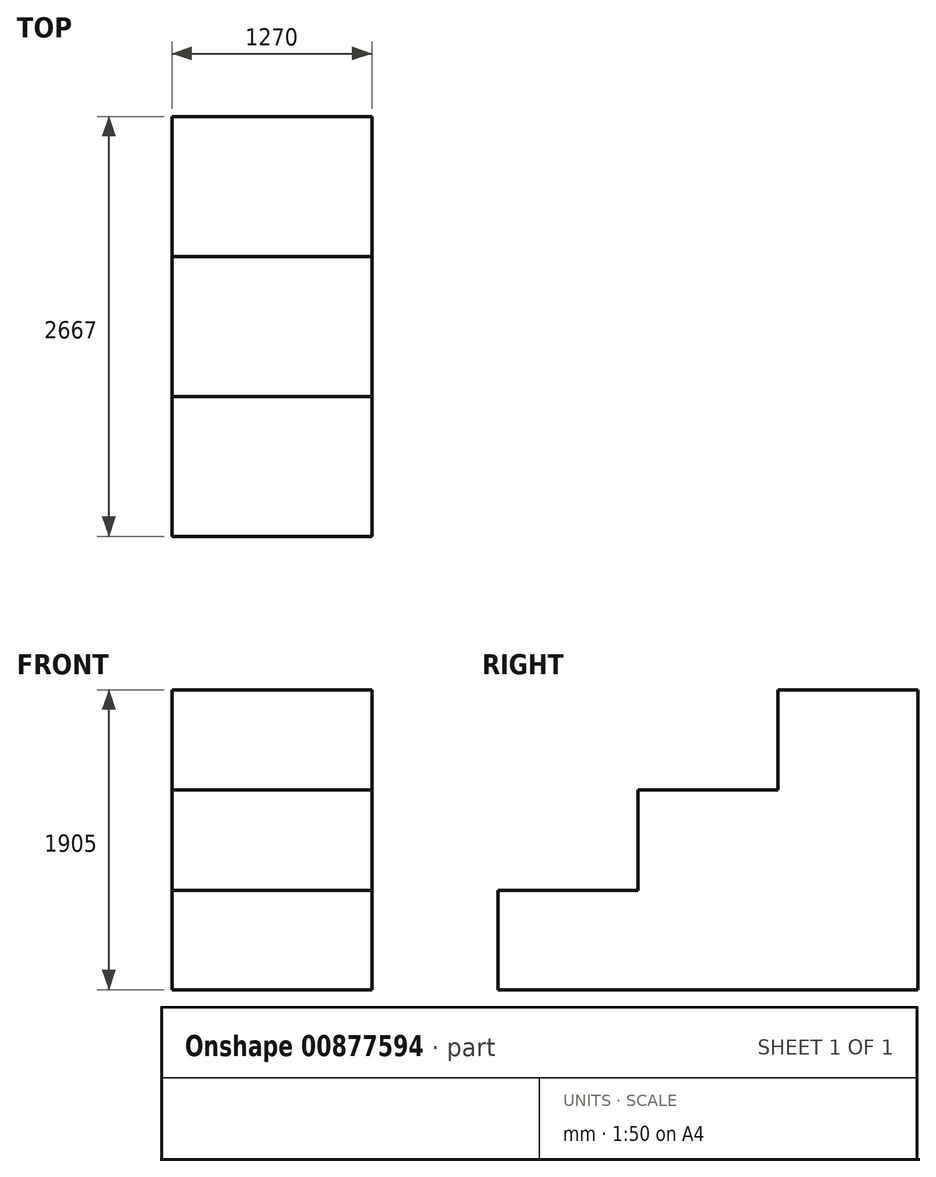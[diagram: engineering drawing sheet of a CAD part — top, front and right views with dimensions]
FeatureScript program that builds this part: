
annotation { "Feature Type Name" : "Feature", "Feature Type Description" : "" }
export const myFeature = defineFeature(function(context is Context, id is Id, definition is map)
    precondition{}
    {
        {
            var Q0;
            Q0=qCreatedBy(makeId("Front.planeOp"),FACE);
            var sketch = newSketch(context, id + "F0", { "sketchPlane" : qUnion([Q0])});
            skLineSegment(sketch, "E0.bottom", {"start": v(0, 0) * mm, "end": v(-1270, 0) * mm});
            skLineSegment(sketch, "E0.top", {"start": v(0, 1905) * mm, "end": v(-1270, 1905) * mm});
            skLineSegment(sketch, "E0.left", {"start": v(0, 0) * mm, "end": v(0, 1905) * mm});
            skLineSegment(sketch, "E0.right", {"start": v(-1270, 0) * mm, "end": v(-1270, 1905) * mm});
            skSolve(sketch);
        }
        {
            var Q0;
            Q0=makeQuery(id+"F0.imprint","IMPRINT",FACE,{"disambiguationData":[TD([[makeQuery(id+"F0.imprint","IMPRINT",EDGE,{"derivedFrom":sQuery(id+"F0.wireOp",EDGE,"E0.bottom")}),-1.0]])]});
            extrude(context, id + "F1", {"entities" : qUnion([Q0]), "depth" : 2667 * mm, "offsetDistance" : 25.4 * mm});
        }
        {
            var Q0;
            Q0=makeQuery(id+"F1.opExtrude","SWEPT_FACE",FACE,{"disambiguationData":[OSD([sQuery(id+"F0.wireOp",EDGE,"E0.left")])]});
            var sketch = newSketch(context, id + "F2", { "sketchPlane" : qUnion([Q0])});
            skLineSegment(sketch, "E1.bottom", {"start": v(-2667, 1264.99) * mm, "end": v(-1778, 1264.99) * mm});
            skLineSegment(sketch, "E1.top", {"start": v(-2667, 629.99) * mm, "end": v(-1778, 629.99) * mm});
            skLineSegment(sketch, "E1.left", {"start": v(-2667, 1264.99) * mm, "end": v(-2667, 629.99) * mm});
            skLineSegment(sketch, "E1.right", {"start": v(-1778, 1264.99) * mm, "end": v(-1778, 629.99) * mm});
            skSolve(sketch);
        }
        {
            var Q0;
            Q0=makeQuery(id+"F2.imprint","IMPRINT",FACE,{"disambiguationData":[TD([[makeQuery(id+"F2.imprint","IMPRINT",EDGE,{"derivedFrom":sQuery(id+"F2.wireOp",EDGE,"E1.bottom")}),-1.0]])]});
            extrude(context, id + "F3", {"entities" : qUnion([Q0]), "operationType" : NewBodyOperationType.REMOVE, "oppositeDirection" : true, "depth" : 1882.14 * mm, "offsetDistance" : 25.4 * mm});
        }
        {
            var Q0;
            Q0=makeQuery(id+"F1.opExtrude","SWEPT_FACE",FACE,{"disambiguationData":[OSD([sQuery(id+"F0.wireOp",EDGE,"E0.left")])]});
            var sketch = newSketch(context, id + "F4", { "sketchPlane" : qUnion([Q0])});
            skLineSegment(sketch, "E2", {"start": v(-1778, 1264.99) * mm, "end": v(-1778, 1905) * mm});
            skSolve(sketch);
        }
        {
            var Q0;
            {var subQ0=sQuery(id+"F4.wireOp",EDGE,"E2");Q0=makeQuery(id+"F4.imprint","IMPRINT",FACE,{"disambiguationData":[TD([[makeQuery(id+"F4.imprint","IMPRINT",EDGE,{"derivedFrom":subQ0}),1.0]])]});}
            extrude(context, id + "F5", {"entities" : qUnion([Q0]), "operationType" : NewBodyOperationType.REMOVE, "oppositeDirection" : true, "depth" : 2161.54 * mm, "offsetDistance" : 25.4 * mm});
        }
        {
            var Q0;
            Q0=makeQuery(id+"F1.opExtrude","SWEPT_FACE",FACE,{"disambiguationData":[OSD([sQuery(id+"F0.wireOp",EDGE,"E0.left")])]});
            var sketch = newSketch(context, id + "F6", { "sketchPlane" : qUnion([Q0])});
            skLineSegment(sketch, "E3.bottom", {"start": v(-1778, 1267.5) * mm, "end": v(-889, 1267.5) * mm});
            skLineSegment(sketch, "E3.top", {"start": v(-1778, 1905) * mm, "end": v(-889, 1905) * mm});
            skLineSegment(sketch, "E3.left", {"start": v(-1778, 1267.5) * mm, "end": v(-1778, 1905) * mm});
            skLineSegment(sketch, "E3.right", {"start": v(-889, 1267.5) * mm, "end": v(-889, 1905) * mm});
            skSolve(sketch);
        }
        {
            var Q0;
            Q0=makeQuery(id+"F6.imprint","IMPRINT",FACE,{"disambiguationData":[TD([[makeQuery(id+"F6.imprint","IMPRINT",EDGE,{"derivedFrom":sQuery(id+"F6.wireOp",EDGE,"E3.bottom")}),1.0]])]});
            var sketch = newSketch(context, id + "F7", { "sketchPlane" : qUnion([Q0])});
            skSolve(sketch);
        }
        {
            var Q0;
            Q0 = qSketchRegion(id + "F7", true);
            var Q1;
            Q1=makeQuery(id+"F7.imprint","IMPRINT",FACE,{"disambiguationData":[TD([[makeQuery(id+"F7.imprint","IMPRINT",EDGE,{"derivedFrom":makeQuery(id+"F6.imprint","IMPRINT",EDGE,{"derivedFrom":sQuery(id+"F6.wireOp",EDGE,"E3.bottom")})}),1.0]])]});
            extrude(context, id + "F8", {"entities" : qUnion([Q0, Q1]), "operationType" : NewBodyOperationType.REMOVE, "oppositeDirection" : true, "depth" : 2392.68 * mm, "offsetDistance" : 25.4 * mm});
        }
    });
